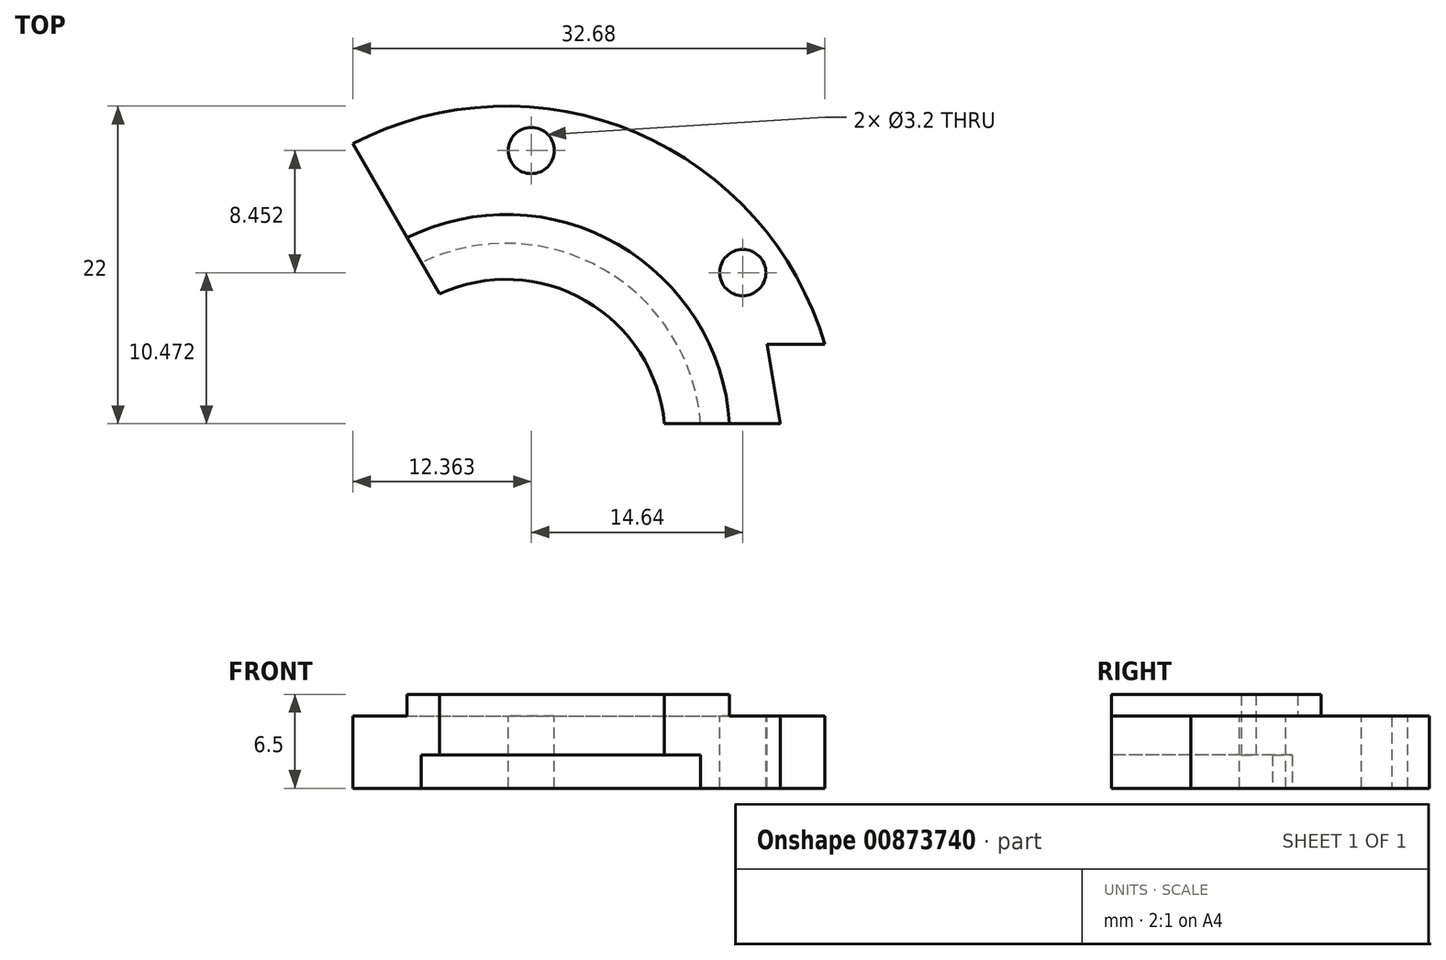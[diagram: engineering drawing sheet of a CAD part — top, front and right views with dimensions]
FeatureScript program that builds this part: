
annotation { "Feature Type Name" : "Feature", "Feature Type Description" : "" }
export const myFeature = defineFeature(function(context is Context, id is Id, definition is map)
    precondition{}
    {
        {
            var Q0;
            Q0=qCreatedBy(makeId("Front.planeOp"),FACE);
            var sketch = newSketch(context, id + "F0", { "sketchPlane" : qUnion([Q0])});
            skLineSegment(sketch, "E0.bottom", {"start": v(15.5, 5) * mm, "end": v(23, 5) * mm});
            skLineSegment(sketch, "E0.top", {"start": v(13.5, 0) * mm, "end": v(23, 0) * mm});
            skLineSegment(sketch, "E0.left", {"start": v(13.5, 2.3) * mm, "end": v(13.5, 0) * mm});
            skLineSegment(sketch, "E0.right", {"start": v(23, 5) * mm, "end": v(23, 0) * mm});
            skLineSegment(sketch, "E1.bottom", {"start": v(11, 6.5) * mm, "end": v(15.5, 6.5) * mm});
            skLineSegment(sketch, "E1.top", {"start": v(11, 2.3) * mm, "end": v(13.5, 2.3) * mm});
            skLineSegment(sketch, "E1.left", {"start": v(11, 6.5) * mm, "end": v(11, 2.3) * mm});
            skLineSegment(sketch, "E1.right", {"start": v(15.5, 6.5) * mm, "end": v(15.5, 5) * mm});
            skLineSegment(sketch, "E2", {"start": v(0, -15.08) * mm, "end": v(0, 22.65) * mm, "construction": true});
            skSolve(sketch);
        }
        {
            var Q0;
            Q0=makeQuery(id+"F0.imprint","IMPRINT",FACE,{"disambiguationData":[TD([[makeQuery(id+"F0.imprint","IMPRINT",EDGE,{"derivedFrom":sQuery(id+"F0.wireOp",EDGE,"E0.bottom")}),-1.0]])]});
            var Q1;
            Q1=sQuery(id+"F0.wireOp",EDGE,"E2");
            revolve(context, id + "F1", {"surfaceOperationType" : NewSurfaceOperationType.NEW, "entities" : qUnion([Q0]), "axis" : qUnion([Q1]), "revolveType" : RevolveType.ONE_DIRECTION, "angle" : 120 * degree});
        }
        {
            var Q0;
            Q0=makeQuery(id+"F1.opRevolve","SWEPT_FACE",FACE,{"disambiguationData":[OSD([sQuery(id+"F0.wireOp",EDGE,"E0.bottom")])]});
            var sketch = newSketch(context, id + "F2", { "sketchPlane" : qUnion([Q0])});
            skCircle(sketch, "E3", {"center": v(-35.33, 45.07) * mm, "radius": 1.6 * mm});
            skLineSegment(sketch, "E4", {"start": v(0, 0) * mm, "end": v(2.34, 26.7) * mm, "construction": true});
            skLineSegment(sketch, "E5", {"start": v(0, 0) * mm, "end": v(20.6, 14.42) * mm, "construction": true});
            skCircle(sketch, "E6", {"center": v(0, 0) * mm, "radius": 20 * mm, "construction": true});
            skCircle(sketch, "E7", {"center": v(1.74, 19.92) * mm, "radius": 1.6 * mm});
            skCircle(sketch, "E8", {"center": v(16.38, 11.47) * mm, "radius": 1.6 * mm});
            skSolve(sketch);
        }
        {
            var Q0;
            Q0=makeQuery(id+"F2.imprint","IMPRINT",FACE,{"disambiguationData":[TD([[makeQuery(id+"F2.imprint","IMPRINT",EDGE,{"derivedFrom":sQuery(id+"F2.wireOp",EDGE,"E7")}),1.0]])]});
            var Q1;
            Q1=makeQuery(id+"F2.imprint","IMPRINT",FACE,{"disambiguationData":[TD([[makeQuery(id+"F2.imprint","IMPRINT",EDGE,{"derivedFrom":sQuery(id+"F2.wireOp",EDGE,"E8")}),1.0]])]});
            var Q2;
            Q2=sQuery(id+"F2.wireOp",EDGE,"QfExOzuu-MPpv-kQ53-jC1U-J9TG8y8jgbir");
            var Q3;
            Q3=sQuery(id+"F2.wireOp",EDGE,"XV8kSXmA-rQH2-eGMI-KoXr-okj3xJ3UZ4DB");
            extrude(context, id + "F3", {"entities" : qUnion([Q0, Q1]), "operationType" : NewBodyOperationType.REMOVE, "surfaceEntities" : qUnion([Q2, Q3]), "endBound" : BoundingType.UP_TO_NEXT, "oppositeDirection" : true, "depth" : 25 * mm, "offsetDistance" : 25 * mm});
        }
        {
            var Q0;
            Q0=makeQuery(id+"F1.opRevolve","CAP_FACE",FACE,{"disambiguationData":[OSD([sQuery(id+"F0.wireOp",EDGE,"E0.bottom"),sQuery(id+"F0.wireOp",EDGE,"E0.top"),sQuery(id+"F0.wireOp",EDGE,"E0.left"),sQuery(id+"F0.wireOp",EDGE,"E0.right"),sQuery(id+"F0.wireOp",EDGE,"E1.bottom"),sQuery(id+"F0.wireOp",EDGE,"E1.top"),sQuery(id+"F0.wireOp",EDGE,"E1.left"),sQuery(id+"F0.wireOp",EDGE,"E1.right")])],"isStart":true});
            cPlane(context, id + "F4", {"entities" : qUnion([Q0]), "cplaneType" : CPlaneType.OFFSET, "offset" : 1 * mm, "oppositeDirection" : true, "width" : 150 * mm, "height" : 150 * mm});
        }
        {
            var Q0;
            Q0=makeQuery(id+"F1.opRevolve","CAP_FACE",FACE,{"disambiguationData":[OSD([sQuery(id+"F0.wireOp",EDGE,"E0.bottom"),sQuery(id+"F0.wireOp",EDGE,"E0.top"),sQuery(id+"F0.wireOp",EDGE,"E0.left"),sQuery(id+"F0.wireOp",EDGE,"E0.right"),sQuery(id+"F0.wireOp",EDGE,"E1.bottom"),sQuery(id+"F0.wireOp",EDGE,"E1.top"),sQuery(id+"F0.wireOp",EDGE,"E1.left"),sQuery(id+"F0.wireOp",EDGE,"E1.right")])],"isStart":false});
            cPlane(context, id + "F5", {"entities" : qUnion([Q0]), "cplaneType" : CPlaneType.OFFSET, "offset" : 1 * mm, "oppositeDirection" : true, "width" : 150 * mm, "height" : 150 * mm});
        }
        {
            var Q0;
            Q0=qCreatedBy(id+"F4.planeOp",FACE);
            var sketch = newSketch(context, id + "F6", { "sketchPlane" : qUnion([Q0])});
            skLineSegment(sketch, "E9.bottom", {"start": v(10.66, 6.87) * mm, "end": v(23.6, 6.87) * mm});
            skLineSegment(sketch, "E9.top", {"start": v(10.66, -0.58) * mm, "end": v(23.6, -0.58) * mm});
            skLineSegment(sketch, "E9.left", {"start": v(10.66, 6.87) * mm, "end": v(10.66, -0.58) * mm});
            skLineSegment(sketch, "E9.right", {"start": v(23.6, 6.87) * mm, "end": v(23.6, -0.58) * mm});
            skSolve(sketch);
        }
        {
            var Q0;
            Q0=makeQuery(id+"F6.imprint","IMPRINT",FACE,{"disambiguationData":[TD([[makeQuery(id+"F6.imprint","IMPRINT",EDGE,{"derivedFrom":sQuery(id+"F6.wireOp",EDGE,"E9.bottom")}),-1.0]])]});
            extrude(context, id + "F7", {"entities" : qUnion([Q0]), "operationType" : NewBodyOperationType.REMOVE, "endBound" : BoundingType.UP_TO_NEXT, "depth" : 25 * mm, "offsetDistance" : 25 * mm});
        }
        {
            var Q0;
            Q0=qCreatedBy(id+"F5.planeOp",FACE);
            var sketch = newSketch(context, id + "F8", { "sketchPlane" : qUnion([Q0])});
            skLineSegment(sketch, "E10.bottom", {"start": v(-10.6, 7.25) * mm, "end": v(-23.6, 7.25) * mm});
            skLineSegment(sketch, "E10.top", {"start": v(-10.6, -0.72) * mm, "end": v(-23.6, -0.72) * mm});
            skLineSegment(sketch, "E10.left", {"start": v(-10.6, 7.25) * mm, "end": v(-10.6, -0.72) * mm});
            skLineSegment(sketch, "E10.right", {"start": v(-23.6, 7.25) * mm, "end": v(-23.6, -0.72) * mm});
            skSolve(sketch);
        }
        {
            var Q0;
            Q0=makeQuery(id+"F8.imprint","IMPRINT",FACE,{"disambiguationData":[TD([[makeQuery(id+"F8.imprint","IMPRINT",EDGE,{"derivedFrom":sQuery(id+"F8.wireOp",EDGE,"E10.bottom")}),1.0]])]});
            extrude(context, id + "F9", {"entities" : qUnion([Q0]), "operationType" : NewBodyOperationType.REMOVE, "endBound" : BoundingType.UP_TO_NEXT, "depth" : 25 * mm, "offsetDistance" : 25 * mm});
        }
        {
            var Q0;
            Q0=makeQuery(id+"F1.opRevolve","SWEPT_FACE",FACE,{"disambiguationData":[OSD([sQuery(id+"F0.wireOp",EDGE,"E0.bottom")])]});
            var sketch = newSketch(context, id + "F10", { "sketchPlane" : qUnion([Q0])});
            skLineSegment(sketch, "E11", {"start": v(22.98, 1) * mm, "end": v(18.98, 1) * mm});
            skLineSegment(sketch, "E12", {"start": v(18.98, 1) * mm, "end": v(18.06, 6.5) * mm});
            skLineSegment(sketch, "E13", {"start": v(18.06, 6.5) * mm, "end": v(22.06, 6.5) * mm});
            skLineSegment(sketch, "E14", {"start": v(22.06, 6.5) * mm, "end": v(23.69, 6.5) * mm});
            skLineSegment(sketch, "E15", {"start": v(23.69, 6.5) * mm, "end": v(23.69, 1) * mm});
            skLineSegment(sketch, "E16", {"start": v(23.69, 1) * mm, "end": v(22.98, 1) * mm});
            skSolve(sketch);
        }
        {
            var Q0;
            {var subQ0=sQuery(id+"F10.wireOp",EDGE,"E11");Q0=makeQuery(id+"F10.imprint","IMPRINT",FACE,{"disambiguationData":[TD([[makeQuery(id+"F10.imprint","IMPRINT",EDGE,{"derivedFrom":subQ0}),1.0]])]});}
            var Q1;
            {var subQ0=sQuery(id+"F10.wireOp",EDGE,"E14");Q1=makeQuery(id+"F10.imprint","IMPRINT",FACE,{"disambiguationData":[TD([[makeQuery(id+"F10.imprint","IMPRINT",EDGE,{"derivedFrom":subQ0}),-1.0]])]});}
            extrude(context, id + "F11", {"entities" : qUnion([Q0, Q1]), "operationType" : NewBodyOperationType.REMOVE, "endBound" : BoundingType.UP_TO_NEXT, "oppositeDirection" : true, "depth" : 25 * mm, "offsetDistance" : 25 * mm});
        }
    });
